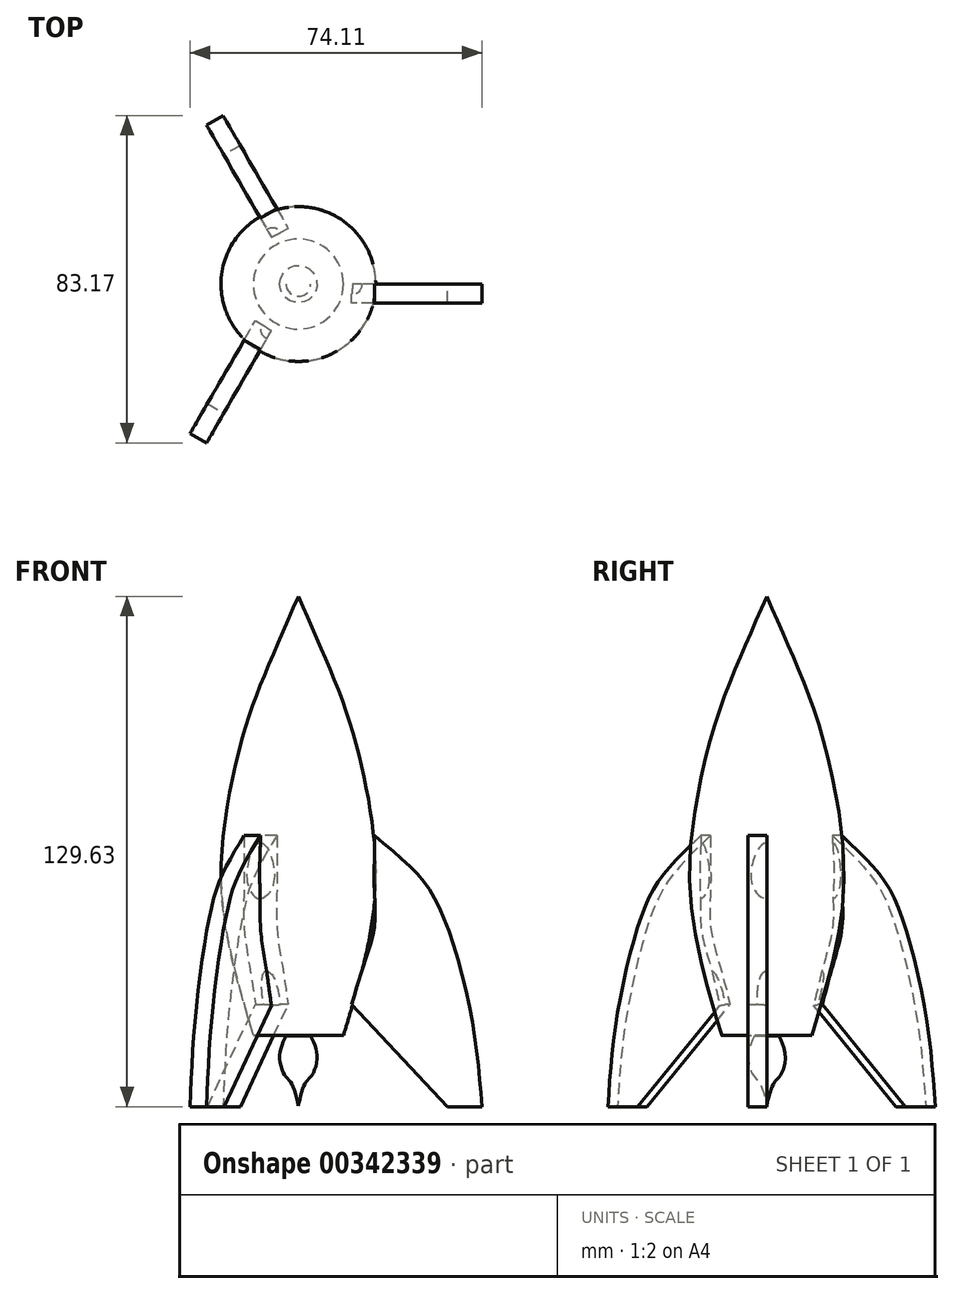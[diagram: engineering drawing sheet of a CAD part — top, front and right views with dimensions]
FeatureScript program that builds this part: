
annotation { "Feature Type Name" : "Feature", "Feature Type Description" : "" }
export const myFeature = defineFeature(function(context is Context, id is Id, definition is map)
    precondition{}
    {
        {
            var Q0;
            Q0=qCreatedBy(makeId("Front.planeOp"),FACE);
            var sketch = newSketch(context, id + "F0", { "sketchPlane" : qUnion([Q0])});
            skFitSpline(sketch, "E0", {"points": [v(0, 49.32) * mm, v(-8.52, 29.6) * mm, v(-14.37, 12.79) * mm, v(-19.48, -15.7) * mm, v(-17.78, -38.6) * mm, v(-11.45, -62.23) * mm], "startDerivative": vector(-46.89, -106.13) * mm, "endDerivative": vector(34.7, -116.04) * mm});
            skLineSegment(sketch, "E1", {"start": v(-11.45, -62.23) * mm, "end": v(0, -62.23) * mm});
            skLineSegment(sketch, "E2", {"start": v(0, -62.23) * mm, "end": v(0, 49.32) * mm});
            skSolve(sketch);
        }
        {
            var Q0;
            Q0=qCreatedBy(makeId("Front.planeOp"),FACE);
            var sketch = newSketch(context, id + "F1", { "sketchPlane" : qUnion([Q0])});
            skLineSegment(sketch, "E3", {"start": v(0, 49.56) * mm, "end": v(0, -61.74) * mm, "construction": true});
            skSolve(sketch);
        }
        {
            var Q0;
            Q0=makeQuery(id+"F0.imprint","IMPRINT",FACE,{"disambiguationData":[TD([[makeQuery(id+"F0.imprint","IMPRINT",EDGE,{"derivedFrom":sQuery(id+"F0.wireOp",EDGE,"E0")}),1.0]])]});
            var Q1;
            Q1=sQuery(id+"F0.wireOp",EDGE,"E2");
            revolve(context, id + "F2", {"entities" : qUnion([Q0]), "axis" : qUnion([Q1]), "revolveType" : RevolveType.FULL});
        }
        {
            var Q0;
            Q0=qCreatedBy(makeId("Front.planeOp"),FACE);
            var sketch = newSketch(context, id + "F3", { "sketchPlane" : qUnion([Q0])});
            skFitSpline(sketch, "E4", {"points": [v(-3.12, -62.27) * mm, v(-4.75, -67.47) * mm, v(-3.45, -72.35) * mm, v(-1.82, -74.3) * mm, v(0, -80.31) * mm], "startDerivative": vector(-8.73, -18.63) * mm, "endDerivative": vector(5.42, -24.67) * mm});
            skLineSegment(sketch, "E5", {"start": v(-3.12, -62.27) * mm, "end": v(0, -62.27) * mm});
            skLineSegment(sketch, "E6", {"start": v(0, -62.27) * mm, "end": v(-0.04, -80.48) * mm});
            skSolve(sketch);
        }
        {
            var Q0;
            {var subQ0=sQuery(id+"F3.wireOp",EDGE,"E5");Q0=makeQuery(id+"F3.imprint","IMPRINT",FACE,{"disambiguationData":[TD([[makeQuery(id+"F3.imprint","IMPRINT",EDGE,{"derivedFrom":subQ0}),-1.0]])]});}
            var Q1;
            Q1=sQuery(id+"F3.wireOp",EDGE,"E6");
            revolve(context, id + "F4", {"entities" : qUnion([Q0]), "axis" : qUnion([Q1]), "revolveType" : RevolveType.FULL});
        }
        {
            var Q0;
            Q0=qCreatedBy(makeId("Front.planeOp"),FACE);
            var sketch = newSketch(context, id + "F5", { "sketchPlane" : qUnion([Q0])});
            skFitSpline(sketch, "E7", {"points": [v(19.28, -11.42) * mm, v(30.5, -21.53) * mm, v(36.78, -31.92) * mm, v(43.89, -57.07) * mm, v(46.62, -80.3) * mm], "startDerivative": vector(54.95, -45.35) * mm, "endDerivative": vector(6.24, -80.03) * mm});
            skLineSegment(sketch, "E8", {"start": v(46.62, -80.3) * mm, "end": v(37.88, -80.3) * mm});
            skLineSegment(sketch, "E9", {"start": v(37.88, -80.3) * mm, "end": v(13.54, -54.34) * mm});
            skFitSpline(sketch, "E10", {"points": [v(19.28, -11.42) * mm, v(19.28, -17.7) * mm, v(19.28, -24.81) * mm, v(19.28, -34.65) * mm, v(16.55, -44.5) * mm, v(13.54, -54.34) * mm], "startDerivative": vector(0.2, -36.75) * mm, "endDerivative": vector(-13.2, -45.3) * mm});
            skSolve(sketch);
        }
        {
            var Q0;
            Q0=makeQuery(id+"F5.imprint","IMPRINT",FACE,{"disambiguationData":[TD([[makeQuery(id+"F5.imprint","IMPRINT",EDGE,{"derivedFrom":sQuery(id+"F5.wireOp",EDGE,"E7")}),-1.0]])]});
            extrude(context, id + "F6", {"entities" : qUnion([Q0]), "operationType" : NewBodyOperationType.ADD, "depth" : 4.83 * mm});
        }
        {
            var Q0;
            Q0=makeQuery(id+"F2.opRevolve","SWEPT_BODY",BODY,{"disambiguationData":[OSD([sQuery(id+"F0.wireOp",EDGE,"E0"),sQuery(id+"F0.wireOp",EDGE,"E1"),sQuery(id+"F0.wireOp",EDGE,"E2")])]});
            var Q1;
            Q1=sQuery(id+"F1.wireOp",EDGE,"E3");
            circularPattern(context, id + "F7", {"entities" : qUnion([Q0]), "axis" : qUnion([Q1]), "angle" : 360 * degree, "instanceCount" : 3, "equalSpace" : true});
        }
    });
